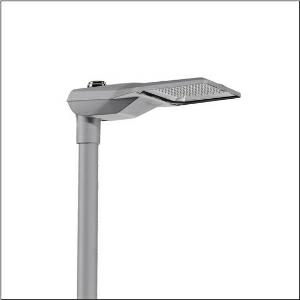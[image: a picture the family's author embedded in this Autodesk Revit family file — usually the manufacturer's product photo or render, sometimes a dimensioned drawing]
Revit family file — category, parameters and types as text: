
# Revit family: streetlight_sl_21_midi___pl52_5xe7h37n08lb_6d16
name_source: partatom
category: Lighting Fixtures
units: mm (PartAtom-declared; Revit-internal decimal feet)

## family parameters
Cut with Voids When Loaded = No
Host = Face
Light Source = No
Part Type = Normal
Room Calculation Point = No
Round Connector Dimension = Use Diameter
Shared = No

## types (1)
- --- (1 x LED, 14100 lm, 98.3 W, 3000K)
    Apparent Load = 98 VA
    CIE Flux Codes = 27 59 98 100 100
    Color Rendering = 70
    Color Temperature = 3000K
    Default Elevation = 1800 mm
    Description = Streetlight SL 21 midi, mast luminaire, primary light control with lens, of PMMA, primary optical cover: cover, of toughened safety glass, transparent, light distribution: PL52, light emission: direct distribution, primary light characteristic: asymmetric, installation type: side-entry, LED, 3G 2.5mm², High Power LED, rated luminous flux: 14.100lm, luminous efficacy: 143lm/W, light colour: 730, colour temperature: 3000K, control gear: NEMA (7pin), control: overheat protection, pre-setting: linear dimming characteristic, constant luminous flux control, time-dependent luminous flux control, flexible luminous flux parameterisation, mains connection: 220..240V, AC, 50/60Hz, connection cable pre-assembled, cable length: 10,5m, wiring characteristics: H05VV-F, start of lifetime: 98W, end of service life: 101W, reduction: 45W, luminaire housing, of diecast aluminium (EN AC-44300), powder-coated, SITECO metallic grey (DB 702S), corrosivity category C5 high according to DIN EN ISO 12944, multi-level sealing system, sealing non-destructively replaceable, inclination adjustable: 0°, 5°, 10°, 15°, length: 644mm, width: 335mm, height: 110mm, spigot size: 42mm (side-entry), mounting height: 4..8m, protection rating (complete): IP66, insulation class (complete): insulation class I (protective earthing), certification: CE, ENEC, ENEC+, VDE, impact resistance: IK10, permissible operating ambient temperature for outdoor applications: -40..+50°C, standard-compliant lighting for roads and squares, packaging unit: 1 piece

Light Distribution: PL52
    Height = 111 mm
    Lamp = 1 x LED
    Lamp Light Flux = 14100 lm
    Lamp Power = 98.3 W
    Lamp count = 1
    Length = 644 mm
    Luminous efficacy = 143 lm/W
    Manufacturer = Siteco
    ModVariant = No
    Model = 5XE7H37N08LB
    Number of Poles = 1
    OnlyDefault = Yes
    Power Factor = 1
    Product Name = Streetlight SL 21 midi | PL52
    Product group = mast luminaire | pylon top
    ProductGroupID = 6100
    Protection Class = Protection class I
    Protection Degree = IP 66
    RLX_Detail_Level = 1
    RLX_Emergency_Light_Flux = 0 lm
    RLX_Emergency_Type = 0
    RLX_Emergency_Type_DB = No
    RlxData = <blob elided: 36265 chars, md5=5b0eb8ee>
    Socket = socket
    Standby Power = 0 W
    System Light Flux = 14100 lm
    System Power = 98 W
    Type Comments = factory setting: luminous flux: 100 % | dim-lin: 254 | 1020 mA
    Type Image = l_1294377.jpg
    URL = http://relux.com
    VarID = @adj_136421
    Voltage = 0 V
    Weight = 0.00 kg
    Width = 336 mm

## geometry (parser evidence)
native form markers: Blend x4, Sweep x10
no freeform markers — native parametric forms only
